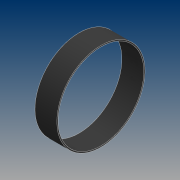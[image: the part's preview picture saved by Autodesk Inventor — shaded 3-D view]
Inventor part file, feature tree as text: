
AUTODESK INVENTOR PART (.ipt)
format: ipt  version: 2021 (Build 250183000, 183)  size: 87,040 bytes
history: native  units: mm
features: extrude x1, sketch x1
ambient origin geometry x8: Origin, YZ Plane, XZ Plane, XY Plane, X Axis, Y Axis, Z Axis, Center Point
bodies: Solid1 (feature_tree)
feature tree (2):
  extrude  "Extrusion1"  Depth=36.0mm
  sketch  "Sketch1"  dims[d0=2.0mm d2=145.0mm d3=36.0mm d4=0.0mm]
